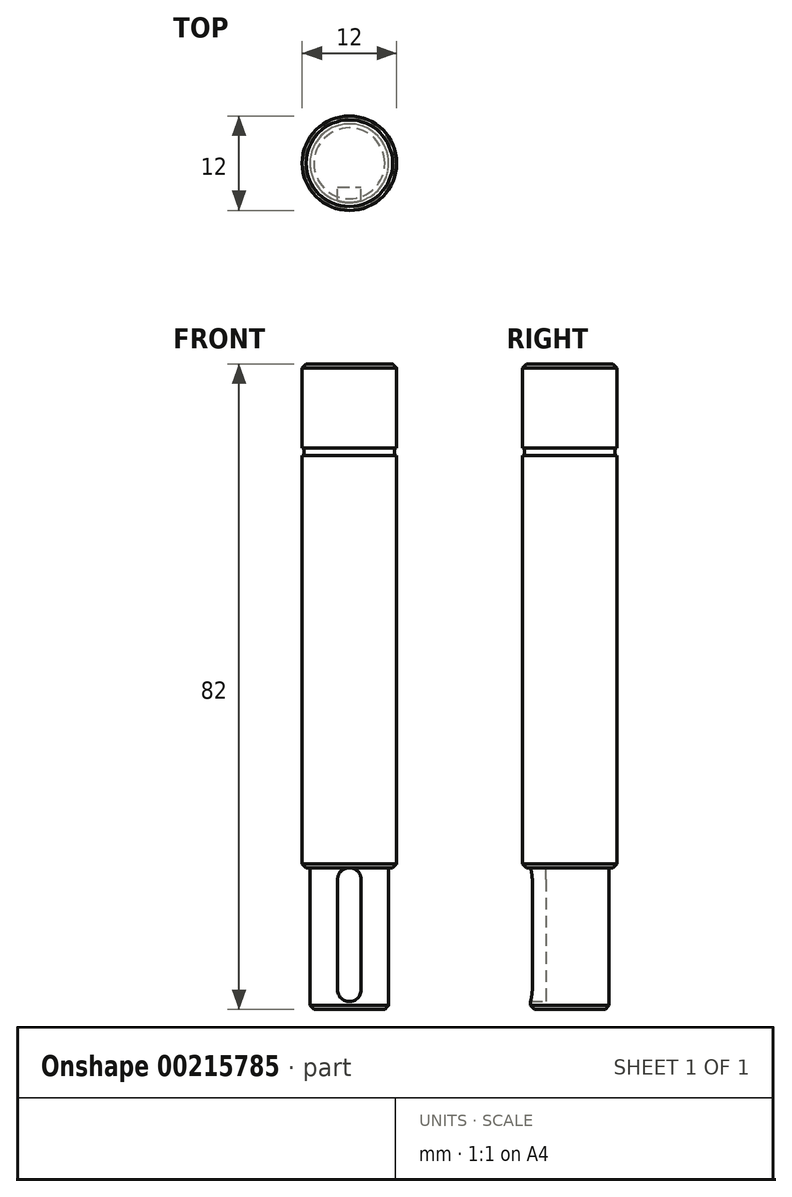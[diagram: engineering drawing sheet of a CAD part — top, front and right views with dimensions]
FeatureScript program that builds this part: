
annotation { "Feature Type Name" : "Feature", "Feature Type Description" : "" }
export const myFeature = defineFeature(function(context is Context, id is Id, definition is map)
    precondition{}
    {
        {
            var Q0;
            Q0=qCreatedBy(makeId("Top.planeOp"),FACE);
            var sketch = newSketch(context, id + "F0", { "sketchPlane" : qUnion([Q0])});
            skCircle(sketch, "E0", {"center": v(0, 0) * mm, "radius": 5 * mm});
            skSolve(sketch);
        }
        {
            var Q0;
            Q0=makeQuery(id+"F0.imprint","IMPRINT",FACE,{"disambiguationData":[TD([[makeQuery(id+"F0.imprint","IMPRINT",EDGE,{"derivedFrom":sQuery(id+"F0.wireOp",EDGE,"E0")}),1.0]])]});
            extrude(context, id + "F1", {"entities" : qUnion([Q0]), "depth" : 18 * mm});
        }
        {
            var Q0;
            Q0=makeQuery(id+"F1.opExtrude","CAP_FACE",FACE,{"disambiguationData":[OSD([sQuery(id+"F0.wireOp",EDGE,"E0")])],"isStart":false});
            var sketch = newSketch(context, id + "F2", { "sketchPlane" : qUnion([Q0])});
            skCircle(sketch, "E1", {"center": v(0, 0) * mm, "radius": 6 * mm});
            skSolve(sketch);
        }
        {
            var Q0;
            Q0 = qSketchRegion(id + "F2", true);
            extrude(context, id + "F3", {"entities" : qUnion([Q0]), "operationType" : NewBodyOperationType.ADD, "depth" : 52.4 * mm});
        }
        {
            var Q0;
            Q0=makeQuery(id+"F3.opExtrude","CAP_FACE",FACE,{"disambiguationData":[OSD([sQuery(id+"F2.wireOp",EDGE,"E1")])],"isStart":false});
            var sketch = newSketch(context, id + "F4", { "sketchPlane" : qUnion([Q0])});
            skCircle(sketch, "E2", {"center": v(0, 0) * mm, "radius": 5.75 * mm});
            skSolve(sketch);
        }
        {
            var Q0;
            Q0 = qSketchRegion(id + "F4", true);
            extrude(context, id + "F5", {"entities" : qUnion([Q0]), "operationType" : NewBodyOperationType.ADD, "depth" : .9 * mm});
        }
        {
            var Q0;
            Q0=makeQuery(id+"F5.opExtrude","CAP_FACE",FACE,{"disambiguationData":[OSD([sQuery(id+"F4.wireOp",EDGE,"E2")])],"isStart":false});
            var sketch = newSketch(context, id + "F6", { "sketchPlane" : qUnion([Q0])});
            skCircle(sketch, "E3", {"center": v(0, 0) * mm, "radius": 6 * mm});
            skSolve(sketch);
        }
        {
            var Q0;
            Q0 = qSketchRegion(id + "F6", true);
            extrude(context, id + "F7", {"entities" : qUnion([Q0]), "operationType" : NewBodyOperationType.ADD, "depth" : 10.7 * mm});
        }
        {
            var Q0;
            Q0=makeQuery(id+"F7.opExtrude","CAP_FACE",FACE,{"disambiguationData":[OSD([sQuery(id+"F6.wireOp",EDGE,"E3")])],"isStart":false});
            chamfer(context, id + "F8", {"entities" : qUnion([Q0]), "chamferType" : ChamferType.OFFSET_ANGLE, "width" : .5 * mm, "oppositeDirection" : false, "angle" : 45 * degree, "tangentPropagation" : true});
        }
        {
            var Q0;
            Q0=makeQuery(id+"F3.opExtrude","CAP_EDGE",EDGE,{"disambiguationData":[OSD([sQuery(id+"F2.wireOp",EDGE,"E1")])],"isStart":true});
            chamfer(context, id + "F9", {"entities" : qUnion([Q0]), "chamferType" : ChamferType.OFFSET_ANGLE, "width" : .5 * mm, "oppositeDirection" : false, "angle" : 45 * degree, "tangentPropagation" : true});
        }
        {
            var Q0;
            Q0=makeQuery(id+"F1.opExtrude","CAP_EDGE",EDGE,{"disambiguationData":[OSD([sQuery(id+"F0.wireOp",EDGE,"E0")])],"isStart":true});
            chamfer(context, id + "F10", {"entities" : qUnion([Q0]), "chamferType" : ChamferType.OFFSET_ANGLE, "width" : .5 * mm, "oppositeDirection" : false, "angle" : 45 * degree, "tangentPropagation" : true});
        }
        {
            var Q0;
            Q0=qCreatedBy(makeId("Front.planeOp"),FACE);
            var sketch = newSketch(context, id + "F11", { "sketchPlane" : qUnion([Q0])});
            skLineSegment(sketch, "E4", {"start": v(0, 0) * mm, "end": v(0, 2.5) * mm});
            skLineSegment(sketch, "E5", {"start": v(0, 2.5) * mm, "end": v(0, 16.5) * mm});
            skArc(sketch, "E6", {"start": v(1.5, 16.5) * mm, "mid": v(0, 18) * mm, "end": v(-1.5, 16.5) * mm});
            skArc(sketch, "E7", {"start": v(1.5, 2.5) * mm, "mid": v(0, 1) * mm, "end": v(-1.5, 2.5) * mm});
            skLineSegment(sketch, "E8", {"start": v(-1.5, 16.5) * mm, "end": v(-1.5, 2.5) * mm});
            skLineSegment(sketch, "E9", {"start": v(1.5, 16.5) * mm, "end": v(1.5, 2.5) * mm});
            skSolve(sketch);
        }
        {
            var Q0;
            Q0 = qSketchRegion(id + "F11", true);
            var Q1;
            Q1=sQuery(id+"F11.wireOp",EDGE,"E9");
            var Q2;
            Q2=sQuery(id+"F11.wireOp",EDGE,"E8");
            var Q3;
            Q3=sQuery(id+"F11.wireOp",EDGE,"E6");
            var Q4;
            Q4=sQuery(id+"F11.wireOp",EDGE,"E7");
            extrude(context, id + "F12", {"entities" : qUnion([Q0]), "operationType" : NewBodyOperationType.REMOVE, "surfaceEntities" : qUnion([Q1, Q2, Q3, Q4]), "depth" : 25 * mm, "hasSecondDirection" : true, "secondDirectionOppositeDirection" : false, "secondDirectionDepth" : 3 * mm});
        }
    });
